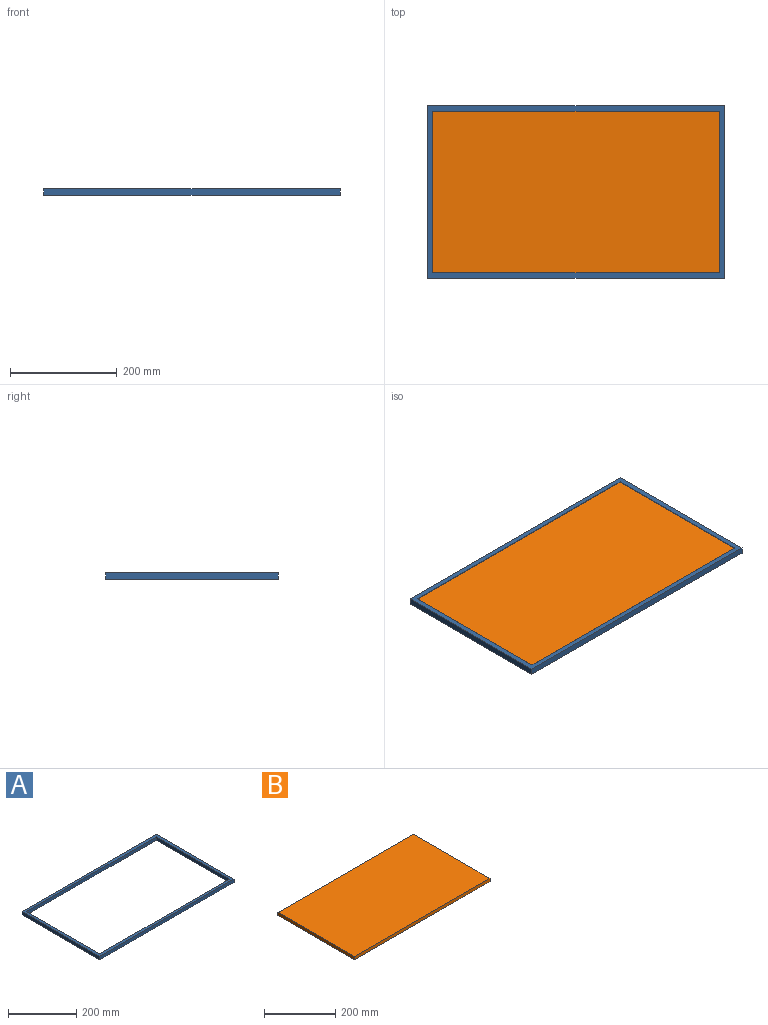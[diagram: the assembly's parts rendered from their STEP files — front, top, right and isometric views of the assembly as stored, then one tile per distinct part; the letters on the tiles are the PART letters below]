
ASSEMBLY  parts=2 mates=1
PART A: 10 faces, bbox 556x323x12 mm
  f0: plane 556x12mm, normal (0,1,0), area 6672mm2, adj f1,f7,f8,f9
  f1: plane 323x12mm, normal (-1,0,0), area 3876mm2, adj f0,f2,f8,f9
  f2: plane 556x12mm, normal (0,-1,0), area 6672mm2, adj f1,f7,f8,f9
  f3: plane 303x12mm, normal (-1,0,0), area 3636mm2, adj f4,f6,f8,f9
  f4: plane 536x12mm, normal (0,1,0), area 6432mm2, adj f3,f5,f8,f9
  f5: plane 303x12mm, normal (1,0,0), area 3636mm2, adj f4,f6,f8,f9
  f6: plane 536x12mm, normal (0,-1,0), area 6432mm2, adj f3,f5,f8,f9
  f7: plane 323x12mm, normal (1,0,0), area 3876mm2, adj f0,f2,f8,f9
  f8: plane 556x323mm, normal (0,0,1), area 17180mm2, adj f0,f1,f2,f3,f4,f5,f6,f7
  f9: plane 556x323mm, normal (0,0,-1), area 17180mm2, adj f0,f1,f2,f3,f4,f5,f6,f7
PART B: 6 faces, bbox 536x303x11 mm
  f0: plane 536x11mm, normal (0,-1,0), area 5896mm2, adj f1,f3,f4,f5
  f1: plane 303x11mm, normal (1,0,0), area 3333mm2, adj f0,f2,f4,f5
  f2: plane 536x11mm, normal (0,1,0), area 5896mm2, adj f1,f3,f4,f5
  f3: plane 303x11mm, normal (-1,0,0), area 3333mm2, adj f0,f2,f4,f5
  f4: plane 536x303mm, normal (0,0,1), area 162408mm2, adj f0,f1,f2,f3
  f5: plane 536x303mm, normal (0,0,-1), area 162408mm2, adj f0,f1,f2,f3
PLACE A at identity
PLACE B at identity
MATE fastened B.f5 <-> A.f9  axis (0,0,-1) through (0,0,0)mm
